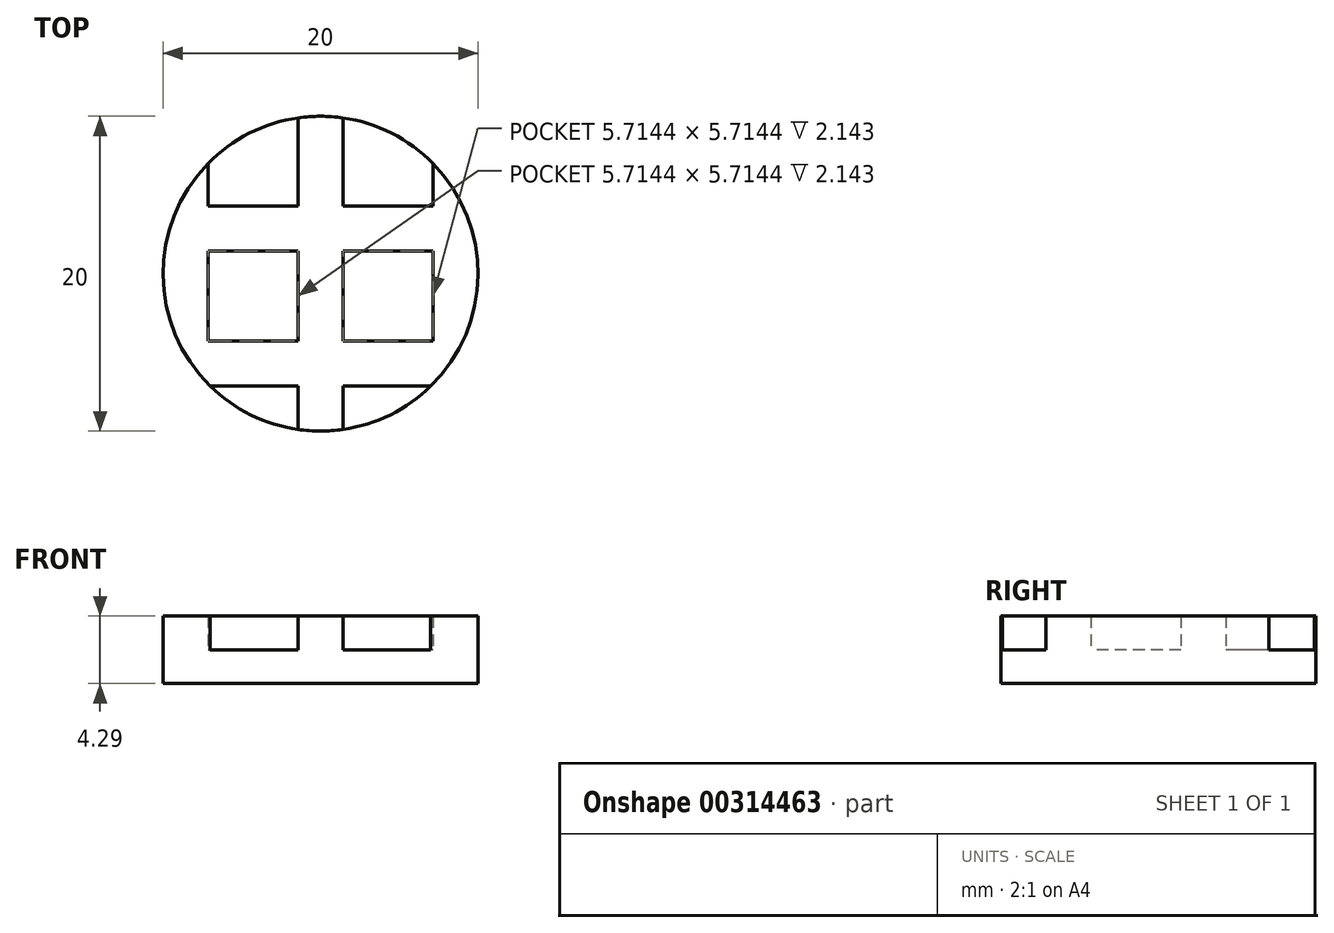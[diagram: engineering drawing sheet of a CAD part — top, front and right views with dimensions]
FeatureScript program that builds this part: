
annotation { "Feature Type Name" : "Feature", "Feature Type Description" : "" }
export const myFeature = defineFeature(function(context is Context, id is Id, definition is map)
    precondition{}
    {
        {
            var Q0;
            Q0=qCreatedBy(makeId("Top.planeOp"),FACE);
            var sketch = newSketch(context, id + "F0", { "sketchPlane" : qUnion([Q0])});
            skCircle(sketch, "E0", {"center": v(0, 0) * mm, "radius": 14 * mm});
            skSolve(sketch);
        }
        {
            var Q0;
            Q0=makeQuery(id+"F0.imprint","IMPRINT",FACE,{"disambiguationData":[TD([[makeQuery(id+"F0.imprint","IMPRINT",EDGE,{"derivedFrom":sQuery(id+"F0.wireOp",EDGE,"E0")}),1.0]])]});
            extrude(context, id + "F1", {"entities" : qUnion([Q0]), "depth" : 3 * mm});
        }
        {
            var Q0;
            Q0=makeQuery(id+"F1.opExtrude","CAP_FACE",FACE,{"disambiguationData":[OSD([sQuery(id+"F0.wireOp",EDGE,"E0")])],"isStart":false});
            var sketch = newSketch(context, id + "F2", { "sketchPlane" : qUnion([Q0])});
            skLineSegment(sketch, "E1.bottom", {"start": v(-10, 14) * mm, "end": v(-2, 14) * mm});
            skLineSegment(sketch, "E1.top", {"start": v(-10, 6) * mm, "end": v(-2, 6) * mm});
            skLineSegment(sketch, "E1.left", {"start": v(-10, 14) * mm, "end": v(-10, 6) * mm});
            skLineSegment(sketch, "E1.right", {"start": v(-2, 14) * mm, "end": v(-2, 6) * mm});
            skLineSegment(sketch, "E2.1.0.0", {"start": v(2, 6) * mm, "end": v(10, 6) * mm});
            skLineSegment(sketch, "E2.1.0.1", {"start": v(2, 14) * mm, "end": v(2, 6) * mm});
            skLineSegment(sketch, "E2.1.0.2", {"start": v(10, 14) * mm, "end": v(10, 6) * mm});
            skLineSegment(sketch, "E2.1.0.3", {"start": v(2, 14) * mm, "end": v(10, 14) * mm});
            skLineSegment(sketch, "E2.2.0.0", {"start": v(14, 6) * mm, "end": v(22, 6) * mm});
            skLineSegment(sketch, "E2.2.0.1", {"start": v(14, 14) * mm, "end": v(14, 6) * mm});
            skLineSegment(sketch, "E2.2.0.2", {"start": v(22, 14) * mm, "end": v(22, 6) * mm});
            skLineSegment(sketch, "E2.2.0.3", {"start": v(14, 14) * mm, "end": v(22, 14) * mm});
            skLineSegment(sketch, "E2.direction1", {"start": v(-10, 6) * mm, "end": v(2, 6) * mm, "construction": true});
            skLineSegment(sketch, "E3.0.3.0", {"start": v(26, 6) * mm, "end": v(34, 6) * mm});
            skLineSegment(sketch, "E3.3.3.0", {"start": v(26, 14) * mm, "end": v(26, 6) * mm});
            skLineSegment(sketch, "E3.6.3.0", {"start": v(34, 14) * mm, "end": v(34, 6) * mm});
            skLineSegment(sketch, "E3.9.3.0", {"start": v(26, 14) * mm, "end": v(34, 14) * mm});
            skLineSegment(sketch, "E4.0.4.0", {"start": v(38, 6) * mm, "end": v(46, 6) * mm});
            skLineSegment(sketch, "E4.3.4.0", {"start": v(38, 14) * mm, "end": v(38, 6) * mm});
            skLineSegment(sketch, "E4.6.4.0", {"start": v(46, 14) * mm, "end": v(46, 6) * mm});
            skLineSegment(sketch, "E4.9.4.0", {"start": v(38, 14) * mm, "end": v(46, 14) * mm});
            skLineSegment(sketch, "E5.0.5.0", {"start": v(50, 6) * mm, "end": v(58, 6) * mm});
            skLineSegment(sketch, "E5.3.5.0", {"start": v(50, 14) * mm, "end": v(50, 6) * mm});
            skLineSegment(sketch, "E5.6.5.0", {"start": v(58, 14) * mm, "end": v(58, 6) * mm});
            skLineSegment(sketch, "E5.9.5.0", {"start": v(50, 14) * mm, "end": v(58, 14) * mm});
            skLineSegment(sketch, "E6.0.6.0", {"start": v(62, 6) * mm, "end": v(70, 6) * mm});
            skLineSegment(sketch, "E6.3.6.0", {"start": v(62, 14) * mm, "end": v(62, 6) * mm});
            skLineSegment(sketch, "E6.6.6.0", {"start": v(70, 14) * mm, "end": v(70, 6) * mm});
            skLineSegment(sketch, "E6.9.6.0", {"start": v(62, 14) * mm, "end": v(70, 14) * mm});
            skLineSegment(sketch, "E6.0.7.0", {"start": v(74, 6) * mm, "end": v(82, 6) * mm});
            skLineSegment(sketch, "E6.3.7.0", {"start": v(74, 14) * mm, "end": v(74, 6) * mm});
            skLineSegment(sketch, "E6.6.7.0", {"start": v(82, 14) * mm, "end": v(82, 6) * mm});
            skLineSegment(sketch, "E6.9.7.0", {"start": v(74, 14) * mm, "end": v(82, 14) * mm});
            skLineSegment(sketch, "E7.1.0.0", {"start": v(14, 2) * mm, "end": v(14, -6) * mm});
            skLineSegment(sketch, "E7.1.0.1", {"start": v(-22, -6) * mm, "end": v(-10, -6) * mm, "construction": true});
            skLineSegment(sketch, "E7.1.0.2", {"start": v(-2, 2) * mm, "end": v(-2, -6) * mm});
            skLineSegment(sketch, "E7.1.0.3", {"start": v(2, 2) * mm, "end": v(2, -6) * mm});
            skLineSegment(sketch, "E7.1.0.4", {"start": v(14, -6) * mm, "end": v(22, -6) * mm});
            skLineSegment(sketch, "E7.1.0.5", {"start": v(58, 2) * mm, "end": v(58, -6) * mm});
            skLineSegment(sketch, "E7.1.0.6", {"start": v(50, -6) * mm, "end": v(58, -6) * mm});
            skLineSegment(sketch, "E7.1.0.7", {"start": v(-10, 2) * mm, "end": v(-10, -6) * mm});
            skLineSegment(sketch, "E7.1.0.8", {"start": v(38, 2) * mm, "end": v(38, -6) * mm});
            skLineSegment(sketch, "E7.1.0.9", {"start": v(70, 2) * mm, "end": v(70, -6) * mm});
            skLineSegment(sketch, "E7.1.0.10", {"start": v(22, 2) * mm, "end": v(22, -6) * mm});
            skLineSegment(sketch, "E7.1.0.11", {"start": v(-10, -6) * mm, "end": v(-2, -6) * mm});
            skLineSegment(sketch, "E7.1.0.12", {"start": v(50, 2) * mm, "end": v(58, 2) * mm});
            skLineSegment(sketch, "E7.1.0.13", {"start": v(26, -6) * mm, "end": v(34, -6) * mm});
            skLineSegment(sketch, "E7.1.0.14", {"start": v(14, 2) * mm, "end": v(22, 2) * mm});
            skLineSegment(sketch, "E7.1.0.15", {"start": v(10, 2) * mm, "end": v(10, -6) * mm});
            skLineSegment(sketch, "E7.1.0.16", {"start": v(26, 2) * mm, "end": v(34, 2) * mm});
            skLineSegment(sketch, "E7.1.0.17", {"start": v(62, 2) * mm, "end": v(62, -6) * mm});
            skLineSegment(sketch, "E7.1.0.18", {"start": v(46, 2) * mm, "end": v(46, -6) * mm});
            skLineSegment(sketch, "E7.1.0.19", {"start": v(62, -6) * mm, "end": v(70, -6) * mm});
            skLineSegment(sketch, "E7.1.0.20", {"start": v(26, 2) * mm, "end": v(26, -6) * mm});
            skLineSegment(sketch, "E7.1.0.21", {"start": v(38, 2) * mm, "end": v(46, 2) * mm});
            skLineSegment(sketch, "E7.1.0.22", {"start": v(-14, 2) * mm, "end": v(-14, -6) * mm});
            skLineSegment(sketch, "E7.1.0.23", {"start": v(-22, 2) * mm, "end": v(-14, 2) * mm});
            skLineSegment(sketch, "E7.1.0.24", {"start": v(2, 2) * mm, "end": v(10, 2) * mm});
            skLineSegment(sketch, "E7.1.0.25", {"start": v(2, -6) * mm, "end": v(10, -6) * mm});
            skLineSegment(sketch, "E7.1.0.26", {"start": v(-10, 2) * mm, "end": v(-2, 2) * mm});
            skLineSegment(sketch, "E7.1.0.27", {"start": v(-22, 2) * mm, "end": v(-22, -6) * mm});
            skLineSegment(sketch, "E7.1.0.28", {"start": v(38, -6) * mm, "end": v(46, -6) * mm});
            skLineSegment(sketch, "E7.1.0.29", {"start": v(62, 2) * mm, "end": v(70, 2) * mm});
            skLineSegment(sketch, "E7.1.0.30", {"start": v(50, 2) * mm, "end": v(50, -6) * mm});
            skLineSegment(sketch, "E7.1.0.31", {"start": v(34, 2) * mm, "end": v(34, -6) * mm});
            skLineSegment(sketch, "E7.1.0.32", {"start": v(-22, -6) * mm, "end": v(-14, -6) * mm});
            skLineSegment(sketch, "E7.2.0.0", {"start": v(2, -10) * mm, "end": v(2, -18) * mm});
            skLineSegment(sketch, "E7.2.0.1", {"start": v(-34, -18) * mm, "end": v(-22, -18) * mm, "construction": true});
            skLineSegment(sketch, "E7.2.0.2", {"start": v(-14, -10) * mm, "end": v(-14, -18) * mm});
            skLineSegment(sketch, "E7.2.0.3", {"start": v(-10, -10) * mm, "end": v(-10, -18) * mm});
            skLineSegment(sketch, "E7.2.0.4", {"start": v(2, -18) * mm, "end": v(10, -18) * mm});
            skLineSegment(sketch, "E7.2.0.5", {"start": v(46, -10) * mm, "end": v(46, -18) * mm});
            skLineSegment(sketch, "E7.2.0.6", {"start": v(38, -18) * mm, "end": v(46, -18) * mm});
            skLineSegment(sketch, "E7.2.0.7", {"start": v(-22, -10) * mm, "end": v(-22, -18) * mm});
            skLineSegment(sketch, "E7.2.0.8", {"start": v(26, -10) * mm, "end": v(26, -18) * mm});
            skLineSegment(sketch, "E7.2.0.9", {"start": v(58, -10) * mm, "end": v(58, -18) * mm});
            skLineSegment(sketch, "E7.2.0.10", {"start": v(10, -10) * mm, "end": v(10, -18) * mm});
            skLineSegment(sketch, "E7.2.0.11", {"start": v(-22, -18) * mm, "end": v(-14, -18) * mm});
            skLineSegment(sketch, "E7.2.0.12", {"start": v(38, -10) * mm, "end": v(46, -10) * mm});
            skLineSegment(sketch, "E7.2.0.13", {"start": v(14, -18) * mm, "end": v(22, -18) * mm});
            skLineSegment(sketch, "E7.2.0.14", {"start": v(2, -10) * mm, "end": v(10, -10) * mm});
            skLineSegment(sketch, "E7.2.0.15", {"start": v(-2, -10) * mm, "end": v(-2, -18) * mm});
            skLineSegment(sketch, "E7.2.0.16", {"start": v(14, -10) * mm, "end": v(22, -10) * mm});
            skLineSegment(sketch, "E7.2.0.17", {"start": v(50, -10) * mm, "end": v(50, -18) * mm});
            skLineSegment(sketch, "E7.2.0.18", {"start": v(34, -10) * mm, "end": v(34, -18) * mm});
            skLineSegment(sketch, "E7.2.0.19", {"start": v(50, -18) * mm, "end": v(58, -18) * mm});
            skLineSegment(sketch, "E7.2.0.20", {"start": v(14, -10) * mm, "end": v(14, -18) * mm});
            skLineSegment(sketch, "E7.2.0.21", {"start": v(26, -10) * mm, "end": v(34, -10) * mm});
            skLineSegment(sketch, "E7.2.0.22", {"start": v(-26, -10) * mm, "end": v(-26, -18) * mm});
            skLineSegment(sketch, "E7.2.0.23", {"start": v(-34, -10) * mm, "end": v(-26, -10) * mm});
            skLineSegment(sketch, "E7.2.0.24", {"start": v(-10, -10) * mm, "end": v(-2, -10) * mm});
            skLineSegment(sketch, "E7.2.0.25", {"start": v(-10, -18) * mm, "end": v(-2, -18) * mm});
            skLineSegment(sketch, "E7.2.0.26", {"start": v(-22, -10) * mm, "end": v(-14, -10) * mm});
            skLineSegment(sketch, "E7.2.0.27", {"start": v(-34, -10) * mm, "end": v(-34, -18) * mm});
            skLineSegment(sketch, "E7.2.0.28", {"start": v(26, -18) * mm, "end": v(34, -18) * mm});
            skLineSegment(sketch, "E7.2.0.29", {"start": v(50, -10) * mm, "end": v(58, -10) * mm});
            skLineSegment(sketch, "E7.2.0.30", {"start": v(38, -10) * mm, "end": v(38, -18) * mm});
            skLineSegment(sketch, "E7.2.0.31", {"start": v(22, -10) * mm, "end": v(22, -18) * mm});
            skLineSegment(sketch, "E7.2.0.32", {"start": v(-34, -18) * mm, "end": v(-26, -18) * mm});
            skLineSegment(sketch, "E7.direction1", {"start": v(-10, 6) * mm, "end": v(-22, -6) * mm, "construction": true});
            skLineSegment(sketch, "E8.0.3.0", {"start": v(-10, -22) * mm, "end": v(-10, -30) * mm});
            skLineSegment(sketch, "E8.3.3.0", {"start": v(-46, -30) * mm, "end": v(-34, -30) * mm, "construction": true});
            skLineSegment(sketch, "E8.6.3.0", {"start": v(-26, -22) * mm, "end": v(-26, -30) * mm});
            skLineSegment(sketch, "E8.9.3.0", {"start": v(-22, -22) * mm, "end": v(-22, -30) * mm});
            skLineSegment(sketch, "E8.12.3.0", {"start": v(-10, -30) * mm, "end": v(-2, -30) * mm});
            skLineSegment(sketch, "E8.15.3.0", {"start": v(34, -22) * mm, "end": v(34, -30) * mm});
            skLineSegment(sketch, "E8.18.3.0", {"start": v(26, -30) * mm, "end": v(34, -30) * mm});
            skLineSegment(sketch, "E8.21.3.0", {"start": v(-34, -22) * mm, "end": v(-34, -30) * mm});
            skLineSegment(sketch, "E8.24.3.0", {"start": v(14, -22) * mm, "end": v(14, -30) * mm});
            skLineSegment(sketch, "E8.27.3.0", {"start": v(46, -22) * mm, "end": v(46, -30) * mm});
            skLineSegment(sketch, "E8.30.3.0", {"start": v(-2, -22) * mm, "end": v(-2, -30) * mm});
            skLineSegment(sketch, "E8.33.3.0", {"start": v(-34, -30) * mm, "end": v(-26, -30) * mm});
            skLineSegment(sketch, "E8.36.3.0", {"start": v(26, -22) * mm, "end": v(34, -22) * mm});
            skLineSegment(sketch, "E8.39.3.0", {"start": v(2, -30) * mm, "end": v(10, -30) * mm});
            skLineSegment(sketch, "E8.42.3.0", {"start": v(-10, -22) * mm, "end": v(-2, -22) * mm});
            skLineSegment(sketch, "E8.45.3.0", {"start": v(-14, -22) * mm, "end": v(-14, -30) * mm});
            skLineSegment(sketch, "E8.48.3.0", {"start": v(2, -22) * mm, "end": v(10, -22) * mm});
            skLineSegment(sketch, "E8.51.3.0", {"start": v(38, -22) * mm, "end": v(38, -30) * mm});
            skLineSegment(sketch, "E8.54.3.0", {"start": v(22, -22) * mm, "end": v(22, -30) * mm});
            skLineSegment(sketch, "E8.57.3.0", {"start": v(38, -30) * mm, "end": v(46, -30) * mm});
            skLineSegment(sketch, "E8.60.3.0", {"start": v(2, -22) * mm, "end": v(2, -30) * mm});
            skLineSegment(sketch, "E8.63.3.0", {"start": v(14, -22) * mm, "end": v(22, -22) * mm});
            skLineSegment(sketch, "E8.66.3.0", {"start": v(-38, -22) * mm, "end": v(-38, -30) * mm});
            skLineSegment(sketch, "E8.69.3.0", {"start": v(-46, -22) * mm, "end": v(-38, -22) * mm});
            skLineSegment(sketch, "E8.72.3.0", {"start": v(-22, -22) * mm, "end": v(-14, -22) * mm});
            skLineSegment(sketch, "E8.75.3.0", {"start": v(-22, -30) * mm, "end": v(-14, -30) * mm});
            skLineSegment(sketch, "E8.78.3.0", {"start": v(-34, -22) * mm, "end": v(-26, -22) * mm});
            skLineSegment(sketch, "E8.81.3.0", {"start": v(-46, -22) * mm, "end": v(-46, -30) * mm});
            skLineSegment(sketch, "E8.84.3.0", {"start": v(14, -30) * mm, "end": v(22, -30) * mm});
            skLineSegment(sketch, "E8.87.3.0", {"start": v(38, -22) * mm, "end": v(46, -22) * mm});
            skLineSegment(sketch, "E8.90.3.0", {"start": v(26, -22) * mm, "end": v(26, -30) * mm});
            skLineSegment(sketch, "E8.93.3.0", {"start": v(10, -22) * mm, "end": v(10, -30) * mm});
            skLineSegment(sketch, "E8.96.3.0", {"start": v(-46, -30) * mm, "end": v(-38, -30) * mm});
            skLineSegment(sketch, "E8.0.4.0", {"start": v(-22, -34) * mm, "end": v(-22, -42) * mm});
            skLineSegment(sketch, "E8.3.4.0", {"start": v(-58, -42) * mm, "end": v(-46, -42) * mm, "construction": true});
            skLineSegment(sketch, "E8.6.4.0", {"start": v(-38, -34) * mm, "end": v(-38, -42) * mm});
            skLineSegment(sketch, "E8.9.4.0", {"start": v(-34, -34) * mm, "end": v(-34, -42) * mm});
            skLineSegment(sketch, "E8.12.4.0", {"start": v(-22, -42) * mm, "end": v(-14, -42) * mm});
            skLineSegment(sketch, "E8.15.4.0", {"start": v(22, -34) * mm, "end": v(22, -42) * mm});
            skLineSegment(sketch, "E8.18.4.0", {"start": v(14, -42) * mm, "end": v(22, -42) * mm});
            skLineSegment(sketch, "E8.21.4.0", {"start": v(-46, -34) * mm, "end": v(-46, -42) * mm});
            skLineSegment(sketch, "E8.24.4.0", {"start": v(2, -34) * mm, "end": v(2, -42) * mm});
            skLineSegment(sketch, "E8.27.4.0", {"start": v(34, -34) * mm, "end": v(34, -42) * mm});
            skLineSegment(sketch, "E8.30.4.0", {"start": v(-14, -34) * mm, "end": v(-14, -42) * mm});
            skLineSegment(sketch, "E8.33.4.0", {"start": v(-46, -42) * mm, "end": v(-38, -42) * mm});
            skLineSegment(sketch, "E8.36.4.0", {"start": v(14, -34) * mm, "end": v(22, -34) * mm});
            skLineSegment(sketch, "E8.39.4.0", {"start": v(-10, -42) * mm, "end": v(-2, -42) * mm});
            skLineSegment(sketch, "E8.42.4.0", {"start": v(-22, -34) * mm, "end": v(-14, -34) * mm});
            skLineSegment(sketch, "E8.45.4.0", {"start": v(-26, -34) * mm, "end": v(-26, -42) * mm});
            skLineSegment(sketch, "E8.48.4.0", {"start": v(-10, -34) * mm, "end": v(-2, -34) * mm});
            skLineSegment(sketch, "E8.51.4.0", {"start": v(26, -34) * mm, "end": v(26, -42) * mm});
            skLineSegment(sketch, "E8.54.4.0", {"start": v(10, -34) * mm, "end": v(10, -42) * mm});
            skLineSegment(sketch, "E8.57.4.0", {"start": v(26, -42) * mm, "end": v(34, -42) * mm});
            skLineSegment(sketch, "E8.60.4.0", {"start": v(-10, -34) * mm, "end": v(-10, -42) * mm});
            skLineSegment(sketch, "E8.63.4.0", {"start": v(2, -34) * mm, "end": v(10, -34) * mm});
            skLineSegment(sketch, "E8.66.4.0", {"start": v(-50, -34) * mm, "end": v(-50, -42) * mm});
            skLineSegment(sketch, "E8.69.4.0", {"start": v(-58, -34) * mm, "end": v(-50, -34) * mm});
            skLineSegment(sketch, "E8.72.4.0", {"start": v(-34, -34) * mm, "end": v(-26, -34) * mm});
            skLineSegment(sketch, "E8.75.4.0", {"start": v(-34, -42) * mm, "end": v(-26, -42) * mm});
            skLineSegment(sketch, "E8.78.4.0", {"start": v(-46, -34) * mm, "end": v(-38, -34) * mm});
            skLineSegment(sketch, "E8.81.4.0", {"start": v(-58, -34) * mm, "end": v(-58, -42) * mm});
            skLineSegment(sketch, "E8.84.4.0", {"start": v(2, -42) * mm, "end": v(10, -42) * mm});
            skLineSegment(sketch, "E8.87.4.0", {"start": v(26, -34) * mm, "end": v(34, -34) * mm});
            skLineSegment(sketch, "E8.90.4.0", {"start": v(14, -34) * mm, "end": v(14, -42) * mm});
            skLineSegment(sketch, "E8.93.4.0", {"start": v(-2, -34) * mm, "end": v(-2, -42) * mm});
            skLineSegment(sketch, "E8.96.4.0", {"start": v(-58, -42) * mm, "end": v(-50, -42) * mm});
            skSolve(sketch);
        }
        {
            var Q0;
            {var subQ1=sQuery(id+"F2.wireOp",EDGE,"E2.1.0.0");Q0=makeQuery(id+"F2.imprint","IMPRINT",FACE,{"disambiguationData":[TD([[makeQuery(id+"F2.imprint","IMPRINT",EDGE,{"derivedFrom":subQ1}),-1.0]])]});}
            extrude(context, id + "F3", {"entities" : qUnion([Q0]), "operationType" : NewBodyOperationType.ADD, "depth" : 3 * mm});
        }
        {
            var Q0;
            Q0=makeQuery(id+"F1.opExtrude","SWEPT_BODY",BODY,{"disambiguationData":[OSD([sQuery(id+"F0.wireOp",EDGE,"E0")])]});
            var Q1;
            Q1=qCreatedBy(makeId("Origin.pointOp"),VERTEX);
            transform(context, id + "F4", {"entities" : qUnion([Q0]), "transformType" : TransformType.SCALE_UNIFORMLY, "scale" : 0.71, "scalePoint" : qUnion([Q1]), "makeCopy" : false});
        }
    });
